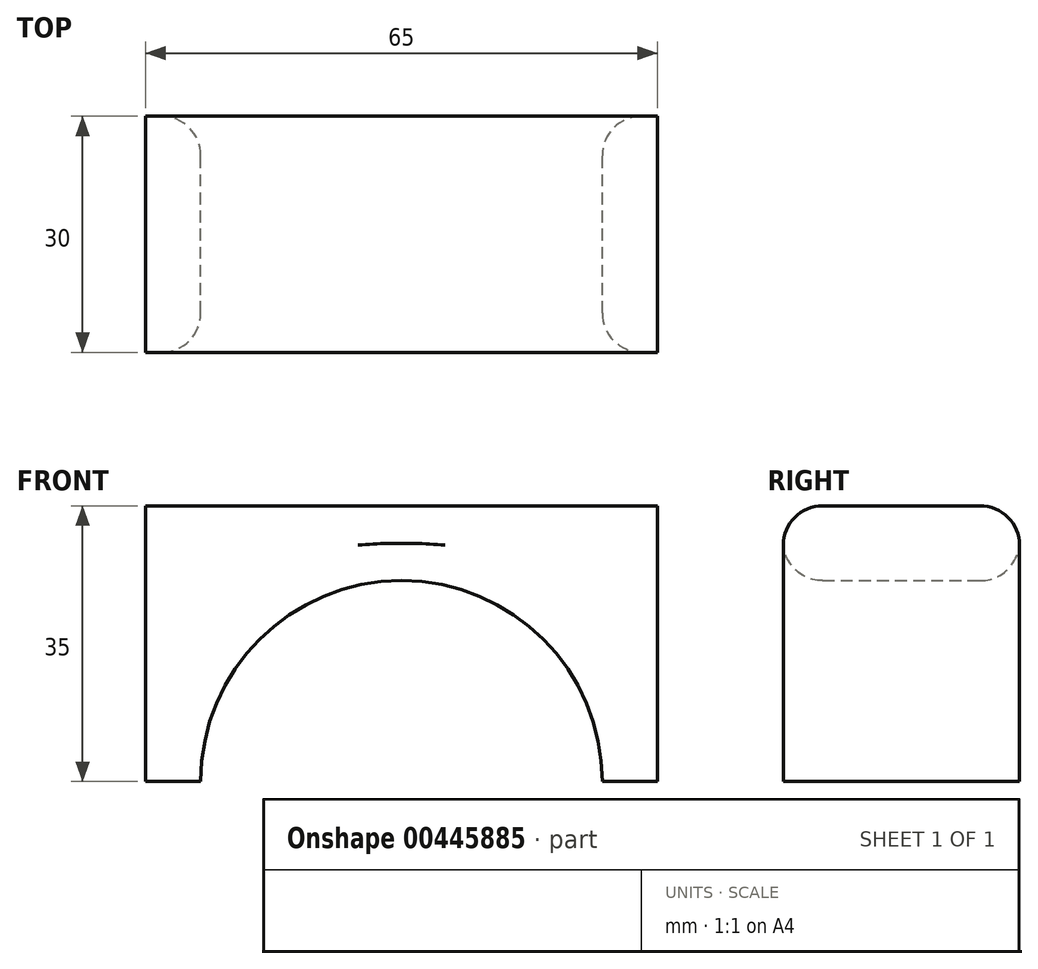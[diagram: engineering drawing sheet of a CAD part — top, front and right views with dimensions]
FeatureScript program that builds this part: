
annotation { "Feature Type Name" : "Feature", "Feature Type Description" : "" }
export const myFeature = defineFeature(function(context is Context, id is Id, definition is map)
    precondition{}
    {
        {
            var Q0;
            Q0=qCreatedBy(makeId("Front.planeOp"),FACE);
            var sketch = newSketch(context, id + "F0", { "sketchPlane" : qUnion([Q0])});
            skLineSegment(sketch, "E0.bottom", {"start": v(0, 0) * mm, "end": v(65, 0) * mm});
            skLineSegment(sketch, "E0.top", {"start": v(0, 35) * mm, "end": v(65, 35) * mm});
            skLineSegment(sketch, "E0.left", {"start": v(0, 0) * mm, "end": v(0, 35) * mm});
            skLineSegment(sketch, "E0.right", {"start": v(65, 0) * mm, "end": v(65, 35) * mm});
            skArc(sketch, "E1", {"start": v(58, 0) * mm, "mid": v(32.5, 25.5) * mm, "end": v(7, 0) * mm});
            skSolve(sketch);
        }
        {
            var Q0;
            Q0=makeQuery(id+"F0.imprint","IMPRINT",FACE,{"disambiguationData":[TD([[makeQuery(id+"F0.imprint","IMPRINT",EDGE,{"derivedFrom":sQuery(id+"F0.wireOp",EDGE,"E0.top")}),-1.0]])]});
            extrude(context, id + "F1", {"entities" : qUnion([Q0]), "depth" : 30 * mm});
        }
        {
            var Q0;
            Q0=makeQuery(id+"F1.opExtrude","CAP_EDGE",EDGE,{"disambiguationData":[OSD([sQuery(id+"F0.wireOp",EDGE,"E0.top")])],"isStart":false});
            var Q1;
            Q1=makeQuery(id+"F1.opExtrude","CAP_EDGE",EDGE,{"disambiguationData":[OSD([sQuery(id+"F0.wireOp",EDGE,"E0.top")])],"isStart":true});
            var Q2;
            Q2=makeQuery(id+"F1.opExtrude","CAP_EDGE",EDGE,{"disambiguationData":[OSD([sQuery(id+"F0.wireOp",EDGE,"E1")])],"isStart":false});
            var Q3;
            Q3=makeQuery(id+"F1.opExtrude","CAP_EDGE",EDGE,{"disambiguationData":[OSD([sQuery(id+"F0.wireOp",EDGE,"E1")])],"isStart":true});
            fillet(context, id + "F2", {"entities" : qUnion([Q0, Q1, Q2, Q3]), "radius" : 5 * mm, "tangentPropagation" : true, "allowEdgeOverflow" : false});
        }
    });
